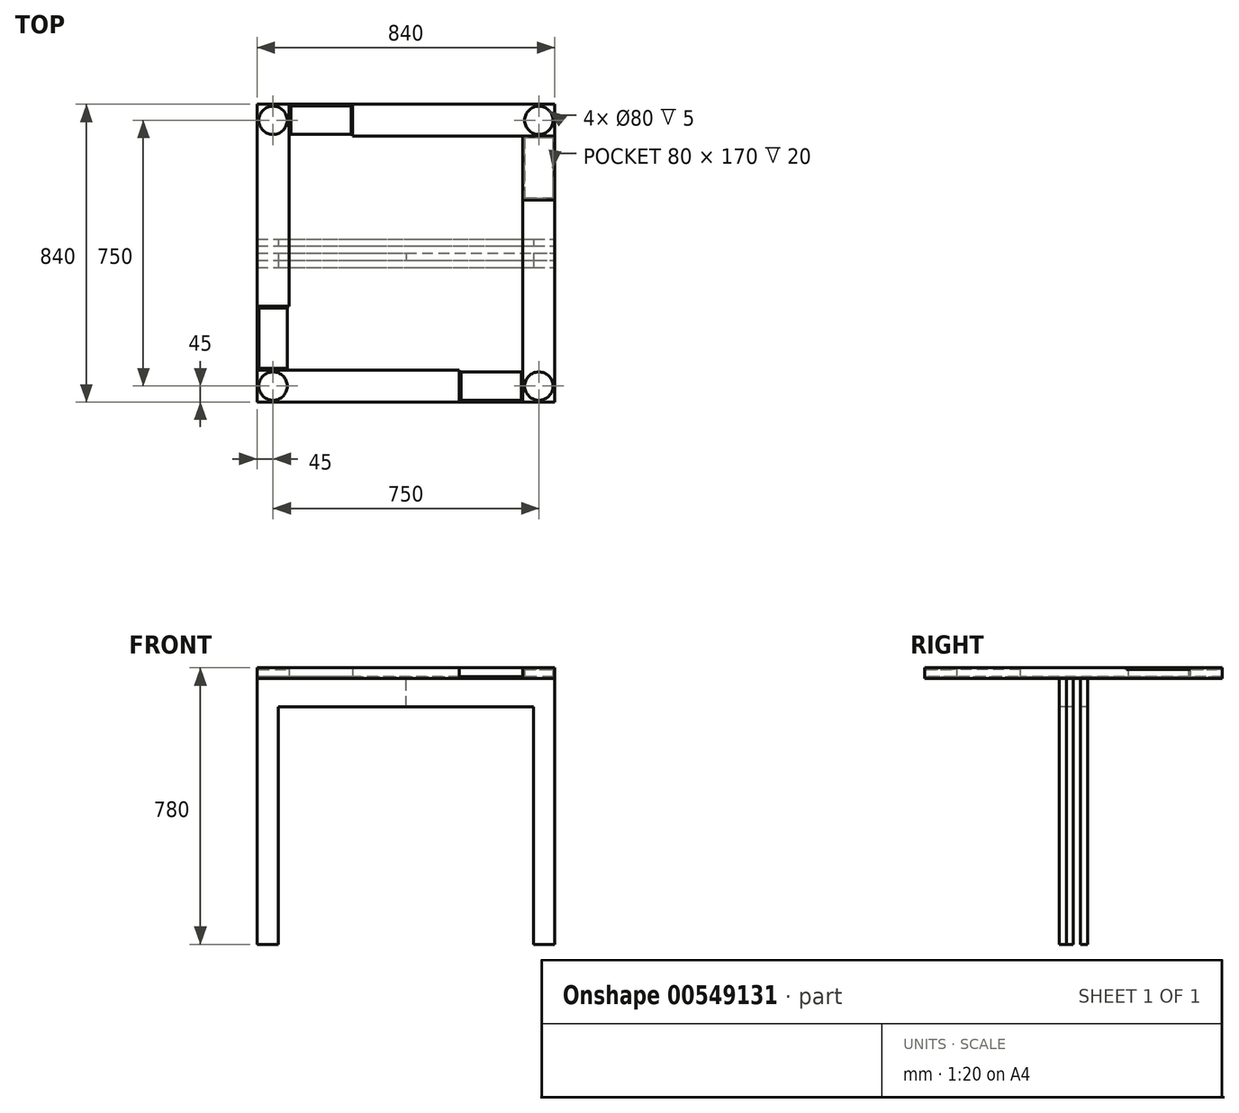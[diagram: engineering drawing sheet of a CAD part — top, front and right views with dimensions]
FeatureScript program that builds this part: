
annotation { "Feature Type Name" : "Feature", "Feature Type Description" : "" }
export const myFeature = defineFeature(function(context is Context, id is Id, definition is map)
    precondition{}
    {
        {
            var Q0;
            Q0=qCreatedBy(makeId("Front.planeOp"),FACE);
            var sketch = newSketch(context, id + "F0", { "sketchPlane" : qUnion([Q0])});
            skLineSegment(sketch, "E0.bottom", {"start": v(420, -15) * mm, "end": v(-420, -15) * mm});
            skLineSegment(sketch, "E0.top", {"start": v(420, 15) * mm, "end": v(-420, 15) * mm});
            skLineSegment(sketch, "E0.left", {"start": v(420, -15) * mm, "end": v(420, 15) * mm});
            skLineSegment(sketch, "E0.right", {"start": v(-420, -15) * mm, "end": v(-420, 15) * mm});
            skPoint(sketch, "E0.middle", {"position": v(0, 0) * mm});
            skLineSegment(sketch, "E1.0", {"start": v(420, -10) * mm, "end": v(-420, -10) * mm});
            skSolve(sketch);
        }
        {
            var Q0;
            Q0=makeQuery(id+"F0.imprint","IMPRINT",FACE,{"disambiguationData":[TD([[makeQuery(id+"F0.imprint","IMPRINT",EDGE,{"derivedFrom":sQuery(id+"F0.wireOp",EDGE,"E0.bottom")}),-1.0]])]});
            extrude(context, id + "F1", {"entities" : qUnion([Q0]), "depth" : 420 * mm, "offsetDistance" : 25 * mm});
        }
        {
            var Q0;
            Q0=makeQuery(id+"F0.imprint","IMPRINT",FACE,{"disambiguationData":[TD([[makeQuery(id+"F0.imprint","IMPRINT",EDGE,{"derivedFrom":sQuery(id+"F0.wireOp",EDGE,"E0.bottom")}),-1.0]])]});
            extrude(context, id + "F2", {"entities" : qUnion([Q0]), "oppositeDirection" : true, "depth" : 420 * mm, "offsetDistance" : 25 * mm});
        }
        {
            var Q0;
            Q0=makeQuery(id+"F2.opExtrude","SWEPT_FACE",FACE,{"disambiguationData":[OSD([sQuery(id+"F0.wireOp",EDGE,"E0.bottom")])]});
            var sketch = newSketch(context, id + "F3", { "sketchPlane" : qUnion([Q0])});
            skLineSegment(sketch, "E2.bottom", {"start": v(330, -330) * mm, "end": v(-330, -330) * mm});
            skLineSegment(sketch, "E2.top", {"start": v(330, 330) * mm, "end": v(-330, 330) * mm});
            skLineSegment(sketch, "E2.left", {"start": v(330, -330) * mm, "end": v(330, 330) * mm});
            skLineSegment(sketch, "E2.right", {"start": v(-330, -330) * mm, "end": v(-330, 330) * mm});
            skPoint(sketch, "E2.middle", {"position": v(0, 0) * mm});
            skLineSegment(sketch, "E3.bottom", {"start": v(-150, -330) * mm, "end": v(-330, -330) * mm});
            skLineSegment(sketch, "E3.top", {"start": v(-150, -420) * mm, "end": v(-330, -420) * mm});
            skLineSegment(sketch, "E3.left", {"start": v(-150, -330) * mm, "end": v(-150, -420) * mm});
            skLineSegment(sketch, "E3.right", {"start": v(-330, -330) * mm, "end": v(-330, -420) * mm});
            skLineSegment(sketch, "E4.bottom", {"start": v(-330, 150) * mm, "end": v(-420, 150) * mm});
            skLineSegment(sketch, "E4.top", {"start": v(-330, 330) * mm, "end": v(-420, 330) * mm});
            skLineSegment(sketch, "E4.left", {"start": v(-330, 150) * mm, "end": v(-330, 330) * mm});
            skLineSegment(sketch, "E4.right", {"start": v(-420, 150) * mm, "end": v(-420, 330) * mm});
            skPoint(sketch, "E5.oppositeSnap0", {"position": v(420, -210) * mm});
            skLineSegment(sketch, "E5.bottom", {"start": v(330, -150) * mm, "end": v(420, -150) * mm});
            skLineSegment(sketch, "E5.top", {"start": v(330, -330) * mm, "end": v(420, -330) * mm});
            skLineSegment(sketch, "E5.left", {"start": v(330, -150) * mm, "end": v(330, -330) * mm});
            skLineSegment(sketch, "E5.right", {"start": v(420, -150) * mm, "end": v(420, -330) * mm});
            skLineSegment(sketch, "E6.bottom", {"start": v(-420, 420) * mm, "end": v(420, 420) * mm});
            skLineSegment(sketch, "E6.top", {"start": v(-420, -420) * mm, "end": v(420, -420) * mm});
            skLineSegment(sketch, "E6.left", {"start": v(-420, -420) * mm, "end": v(-420, 420) * mm});
            skLineSegment(sketch, "E6.right", {"start": v(420, -420) * mm, "end": v(420, 420) * mm});
            skLineSegment(sketch, "E7.bottom", {"start": v(330, 330) * mm, "end": v(150, 330) * mm});
            skLineSegment(sketch, "E7.top", {"start": v(330, 420) * mm, "end": v(150, 420) * mm});
            skLineSegment(sketch, "E7.left", {"start": v(330, 330) * mm, "end": v(330, 420) * mm});
            skLineSegment(sketch, "E7.right", {"start": v(150, 330) * mm, "end": v(150, 420) * mm});
            skLineSegment(sketch, "E8.0", {"start": v(325, 415) * mm, "end": v(155, 415) * mm});
            skLineSegment(sketch, "E8.1", {"start": v(325, 335) * mm, "end": v(325, 415) * mm});
            skLineSegment(sketch, "E8.2", {"start": v(325, 335) * mm, "end": v(155, 335) * mm});
            skLineSegment(sketch, "E8.3", {"start": v(155, 335) * mm, "end": v(155, 415) * mm});
            skLineSegment(sketch, "E9.0", {"start": v(-415, 155) * mm, "end": v(-415, 325) * mm});
            skLineSegment(sketch, "E9.1", {"start": v(-335, 155) * mm, "end": v(-415, 155) * mm});
            skLineSegment(sketch, "E9.2", {"start": v(-335, 155) * mm, "end": v(-335, 325) * mm});
            skLineSegment(sketch, "E9.3", {"start": v(-335, 325) * mm, "end": v(-415, 325) * mm});
            skLineSegment(sketch, "E10.0", {"start": v(-155, -415) * mm, "end": v(-325, -415) * mm});
            skLineSegment(sketch, "E10.1", {"start": v(-155, -335) * mm, "end": v(-155, -415) * mm});
            skLineSegment(sketch, "E10.2", {"start": v(-155, -335) * mm, "end": v(-325, -335) * mm});
            skLineSegment(sketch, "E10.3", {"start": v(-325, -335) * mm, "end": v(-325, -415) * mm});
            skLineSegment(sketch, "E11.0", {"start": v(335, -155) * mm, "end": v(415, -155) * mm});
            skLineSegment(sketch, "E11.1", {"start": v(335, -155) * mm, "end": v(335, -325) * mm});
            skLineSegment(sketch, "E11.2", {"start": v(335, -325) * mm, "end": v(415, -325) * mm});
            skLineSegment(sketch, "E11.3", {"start": v(415, -155) * mm, "end": v(415, -325) * mm});
            skCircle(sketch, "E12", {"center": v(-375, 375) * mm, "radius": 40 * mm});
            skPoint(sketch, "E12.centerSnap0", {"position": v(-375, 330) * mm});
            skCircle(sketch, "E13", {"center": v(375, 375) * mm, "radius": 40 * mm});
            skPoint(sketch, "E13.centerSnap0", {"position": v(330, 375) * mm});
            skPoint(sketch, "E14", {"position": v(375, -150) * mm});
            skCircle(sketch, "E15", {"center": v(375, -375) * mm, "radius": 40 * mm});
            skPoint(sketch, "E15.centerSnap0", {"position": v(-150, -375) * mm});
            skPoint(sketch, "E15.centerSnap1", {"position": v(375, -330) * mm});
            skCircle(sketch, "E16", {"center": v(-375, -375) * mm, "radius": 40 * mm});
            skPoint(sketch, "E16.centerSnap0", {"position": v(-375, 150) * mm});
            skPoint(sketch, "E16.centerSnap1", {"position": v(-330, -375) * mm});
            skSolve(sketch);
        }
        {
            var Q0;
            Q0=makeQuery(id+"F3.imprint","IMPRINT",FACE,{"disambiguationData":[TD([[makeQuery(id+"F3.imprint","IMPRINT",EDGE,{"derivedFrom":sQuery(id+"F3.wireOp",EDGE,"E2.bottom")}),1.0]])]});
            var Q1;
            {var subQ5=sQuery(id+"F3.wireOp",EDGE,"E3.right");Q1=makeQuery(id+"F3.imprint","IMPRINT",FACE,{"disambiguationData":[TD([[makeQuery(id+"F3.imprint","IMPRINT",EDGE,{"derivedFrom":subQ5}),-1.0]])]});}
            var Q2;
            {var subQ0=sQuery(id+"F3.wireOp",EDGE,"E5.bottom");Q2=makeQuery(id+"F3.imprint","IMPRINT",FACE,{"disambiguationData":[TD([[makeQuery(id+"F3.imprint","IMPRINT",EDGE,{"derivedFrom":subQ0}),1.0]])]});}
            var Q3;
            {var subQ1=sQuery(id+"F3.wireOp",EDGE,"E5.bottom");Q3=makeQuery(id+"F3.imprint","IMPRINT",FACE,{"disambiguationData":[TD([[makeQuery(id+"F3.imprint","IMPRINT",EDGE,{"derivedFrom":subQ1}),-1.0]])]});}
            var Q4;
            Q4=makeQuery(id+"F3.imprint","IMPRINT",FACE,{"disambiguationData":[TD([[makeQuery(id+"F3.imprint","IMPRINT",EDGE,{"derivedFrom":sQuery(id+"F3.wireOp",EDGE,"E3.bottom")}),1.0]])]});
            var Q5;
            Q5=makeQuery(id+"F3.imprint","IMPRINT",FACE,{"disambiguationData":[TD([[makeQuery(id+"F3.imprint","IMPRINT",EDGE,{"derivedFrom":sQuery(id+"F3.wireOp",EDGE,"E16")}),1.0]])]});
            var Q6;
            Q6=makeQuery(id+"F3.imprint","IMPRINT",FACE,{"disambiguationData":[TD([[makeQuery(id+"F3.imprint","IMPRINT",EDGE,{"derivedFrom":sQuery(id+"F3.wireOp",EDGE,"E15")}),1.0]])]});
            extrude(context, id + "F4", {"entities" : qUnion([Q0, Q1, Q2, Q3, Q4, Q5, Q6]), "operationType" : NewBodyOperationType.ADD, "oppositeDirection" : true, "depth" : 30 * mm, "offsetDistance" : 25 * mm});
        }
        {
            var Q0;
            {var subQ3=makeQuery(id+"F2.opExtrude","CAP_EDGE",EDGE,{"disambiguationData":[OSD([sQuery(id+"F0.wireOp",EDGE,"E0.bottom")])],"isStart":true});var subQ5=sQuery(id+"F3.wireOp",EDGE,"E6.left");var subQ7=makeQuery(id+"F3.imprint","INTERSECT",VERTEX,{"derivedFrom":[subQ3,subQ5]});Q0=makeQuery(id+"F3.imprint","IMPRINT",FACE,{"disambiguationData":[TD([[makeQuery(id+"F3.imprint","IMPRINT",EDGE,{"disambiguationData":[TD([[subQ7,-1.0]])],"derivedFrom":subQ5}),-1.0]])]});}
            var Q1;
            {var subQ6=sQuery(id+"F3.wireOp",EDGE,"E2.top");Q1=makeQuery(id+"F3.imprint","IMPRINT",FACE,{"disambiguationData":[TD([[makeQuery(id+"F3.imprint","IMPRINT",EDGE,{"derivedFrom":subQ6}),-1.0]])]});}
            var Q2;
            {var subQ5=sQuery(id+"F3.wireOp",EDGE,"E7.left");Q2=makeQuery(id+"F3.imprint","IMPRINT",FACE,{"disambiguationData":[TD([[makeQuery(id+"F3.imprint","IMPRINT",EDGE,{"derivedFrom":subQ5}),-1.0]])]});}
            var Q3;
            Q3=makeQuery(id+"F3.imprint","IMPRINT",FACE,{"disambiguationData":[TD([[makeQuery(id+"F3.imprint","IMPRINT",EDGE,{"derivedFrom":sQuery(id+"F3.wireOp",EDGE,"E12")}),1.0]])]});
            var Q4;
            Q4=makeQuery(id+"F3.imprint","IMPRINT",FACE,{"disambiguationData":[TD([[makeQuery(id+"F3.imprint","IMPRINT",EDGE,{"derivedFrom":sQuery(id+"F3.wireOp",EDGE,"E13")}),1.0]])]});
            var Q5;
            {var subQ0=sQuery(id+"F3.wireOp",EDGE,"E4.left");Q5=makeQuery(id+"F3.imprint","IMPRINT",FACE,{"disambiguationData":[TD([[makeQuery(id+"F3.imprint","IMPRINT",EDGE,{"derivedFrom":subQ0}),1.0]])]});}
            var Q6;
            Q6=makeQuery(id+"F3.imprint","IMPRINT",FACE,{"disambiguationData":[TD([[makeQuery(id+"F3.imprint","IMPRINT",EDGE,{"derivedFrom":sQuery(id+"F3.wireOp",EDGE,"E7.bottom")}),-1.0]])]});
            var Q7;
            {var subQ0=sQuery(id+"F3.wireOp",EDGE,"kfzZb0uT-yHJu-uCjX-pyc7-7eUP6x9U4umR.bottom");var subQ1=sQuery(id+"F3.wireOp",EDGE,"E2.top");var subQ2=sQuery(id+"F3.wireOp",EDGE,"E5.left");var subQ3=sQuery(id+"F3.wireOp",EDGE,"E2.left");var subQ4=sQuery(id+"F3.wireOp",EDGE,"E4.left");var subQ5=sQuery(id+"F3.wireOp",EDGE,"E2.right");Q7=makeQuery(id+"F4.boolean.opBoolean","COPY",FACE,{"disambiguationData":[TD([makeQuery(id+"F4.opExtrude","SWEPT_FACE",FACE,{"disambiguationData":[OSD([subQ1,subQ0])]})])],"derivedFrom":makeQuery(id+"F4.opExtrude","CAP_FACE",FACE,{"disambiguationData":[OSD([sQuery(id+"F3.wireOp",EDGE,"E2.bottom"),subQ1,subQ3,subQ5,sQuery(id+"F3.wireOp",EDGE,"E3.bottom"),subQ0,subQ4,subQ2])],"isStart":false})});}
            extrude(context, id + "F5", {"entities" : qUnion([Q0, Q1, Q2, Q3, Q4, Q5, Q6]), "operationType" : NewBodyOperationType.ADD, "oppositeDirection" : true, "depth" : 30 * mm, "endBoundEntityFace" : qUnion([Q7]), "offsetDistance" : 25 * mm});
        }
        {
            var Q0;
            {var subQ1=sQuery(id+"F3.wireOp",EDGE,"E4.bottom");Q0=makeQuery(id+"F3.imprint","IMPRINT",FACE,{"disambiguationData":[TD([[makeQuery(id+"F3.imprint","IMPRINT",EDGE,{"derivedFrom":subQ1}),-1.0]])]});}
            var Q1;
            Q1=makeQuery(id+"F3.imprint","IMPRINT",FACE,{"disambiguationData":[TD([[makeQuery(id+"F3.imprint","IMPRINT",EDGE,{"derivedFrom":sQuery(id+"F3.wireOp",EDGE,"E9.0")}),-1.0]])]});
            var Q2;
            Q2=makeQuery(id+"F3.imprint","IMPRINT",FACE,{"disambiguationData":[TD([[makeQuery(id+"F3.imprint","IMPRINT",EDGE,{"derivedFrom":sQuery(id+"F3.wireOp",EDGE,"E8.0")}),1.0]])]});
            var Q3;
            Q3=makeQuery(id+"F3.imprint","IMPRINT",FACE,{"disambiguationData":[TD([[makeQuery(id+"F3.imprint","IMPRINT",EDGE,{"derivedFrom":sQuery(id+"F3.wireOp",EDGE,"E7.bottom")}),-1.0]])]});
            var Q4;
            {var subQ1=sQuery(id+"F3.wireOp",EDGE,"E5.bottom");Q4=makeQuery(id+"F3.imprint","IMPRINT",FACE,{"disambiguationData":[TD([[makeQuery(id+"F3.imprint","IMPRINT",EDGE,{"derivedFrom":subQ1}),-1.0]])]});}
            var Q5;
            Q5=makeQuery(id+"F3.imprint","IMPRINT",FACE,{"disambiguationData":[TD([[makeQuery(id+"F3.imprint","IMPRINT",EDGE,{"derivedFrom":sQuery(id+"F3.wireOp",EDGE,"E11.0")}),-1.0]])]});
            var Q6;
            Q6=makeQuery(id+"F3.imprint","IMPRINT",FACE,{"disambiguationData":[TD([[makeQuery(id+"F3.imprint","IMPRINT",EDGE,{"derivedFrom":sQuery(id+"F3.wireOp",EDGE,"E3.bottom")}),1.0]])]});
            var Q7;
            Q7=makeQuery(id+"F3.imprint","IMPRINT",FACE,{"disambiguationData":[TD([[makeQuery(id+"F3.imprint","IMPRINT",EDGE,{"derivedFrom":sQuery(id+"F3.wireOp",EDGE,"E10.0")}),-1.0]])]});
            var Q8;
            Q8=makeQuery(id+"F3.imprint","IMPRINT",FACE,{"disambiguationData":[TD([[makeQuery(id+"F3.imprint","IMPRINT",EDGE,{"derivedFrom":sQuery(id+"F3.wireOp",EDGE,"E12")}),1.0]])]});
            var Q9;
            Q9=makeQuery(id+"F3.imprint","IMPRINT",FACE,{"disambiguationData":[TD([[makeQuery(id+"F3.imprint","IMPRINT",EDGE,{"derivedFrom":sQuery(id+"F3.wireOp",EDGE,"E16")}),1.0]])]});
            var Q10;
            Q10=makeQuery(id+"F3.imprint","IMPRINT",FACE,{"disambiguationData":[TD([[makeQuery(id+"F3.imprint","IMPRINT",EDGE,{"derivedFrom":sQuery(id+"F3.wireOp",EDGE,"E15")}),1.0]])]});
            var Q11;
            Q11=makeQuery(id+"F3.imprint","IMPRINT",FACE,{"disambiguationData":[TD([[makeQuery(id+"F3.imprint","IMPRINT",EDGE,{"derivedFrom":sQuery(id+"F3.wireOp",EDGE,"E13")}),1.0]])]});
            var Q12;
            {var subQ0=sQuery(id+"F3.wireOp",EDGE,"E4.left");Q12=makeQuery(id+"F3.imprint","IMPRINT",FACE,{"disambiguationData":[TD([[makeQuery(id+"F3.imprint","IMPRINT",EDGE,{"derivedFrom":subQ0}),1.0]])]});}
            extrude(context, id + "F6", {"entities" : qUnion([Q0, Q1, Q2, Q3, Q4, Q5, Q6, Q7, Q8, Q9, Q10, Q11, Q12]), "oppositeDirection" : true, "depth" : 5 * mm, "offsetDistance" : 25 * mm});
        }
        {
            var Q0;
            Q0=makeQuery(id+"F6.opExtrude","SWEPT_BODY",BODY,{"disambiguationData":[OSD([sQuery(id+"F3.wireOp",EDGE,"E3.bottom"),sQuery(id+"F3.wireOp",EDGE,"E3.left"),sQuery(id+"F3.wireOp",EDGE,"E3.right"),sQuery(id+"F3.wireOp",EDGE,"E6.top")])]});
            var Q1;
            Q1=makeQuery(id+"F6.opExtrude","SWEPT_BODY",BODY,{"disambiguationData":[OSD([sQuery(id+"F3.wireOp",EDGE,"E4.bottom"),sQuery(id+"F3.wireOp",EDGE,"E4.top"),sQuery(id+"F3.wireOp",EDGE,"E4.left"),sQuery(id+"F3.wireOp",EDGE,"E6.left")])]});
            var Q2;
            Q2=makeQuery(id+"F6.opExtrude","SWEPT_BODY",BODY,{"disambiguationData":[OSD([sQuery(id+"F3.wireOp",EDGE,"E5.bottom"),sQuery(id+"F3.wireOp",EDGE,"E5.top"),sQuery(id+"F3.wireOp",EDGE,"E5.left"),sQuery(id+"F3.wireOp",EDGE,"E6.right")])]});
            var Q3;
            Q3=makeQuery(id+"F6.opExtrude","SWEPT_BODY",BODY,{"disambiguationData":[OSD([sQuery(id+"F3.wireOp",EDGE,"E7.bottom"),sQuery(id+"F3.wireOp",EDGE,"E7.top"),sQuery(id+"F3.wireOp",EDGE,"E7.left"),sQuery(id+"F3.wireOp",EDGE,"E7.right")])]});
            var Q4;
            Q4=makeQuery(id+"F6.opExtrude","SWEPT_BODY",BODY,{"disambiguationData":[OSD([sQuery(id+"F3.wireOp",EDGE,"E16")])]});
            var Q5;
            Q5=makeQuery(id+"F6.opExtrude","SWEPT_BODY",BODY,{"disambiguationData":[OSD([sQuery(id+"F3.wireOp",EDGE,"E12")])]});
            var Q6;
            Q6=makeQuery(id+"F6.opExtrude","SWEPT_BODY",BODY,{"disambiguationData":[OSD([sQuery(id+"F3.wireOp",EDGE,"E13")])]});
            var Q7;
            Q7=makeQuery(id+"F6.opExtrude","SWEPT_BODY",BODY,{"disambiguationData":[OSD([sQuery(id+"F3.wireOp",EDGE,"E15")])]});
            transform(context, id + "F7", {"entities" : qUnion([Q0, Q1, Q2, Q3, Q4, Q5, Q6, Q7]), "transformType" : TransformType.TRANSLATION_3D, "dx" : 0 * mm, "dy" : 0 * mm, "dz" : 25 * mm, "makeCopy" : false});
        }
        {
            var Q0;
            Q0=makeQuery(id+"F6.opExtrude","SWEPT_BODY",BODY,{"disambiguationData":[OSD([sQuery(id+"F3.wireOp",EDGE,"E3.bottom"),sQuery(id+"F3.wireOp",EDGE,"E3.left"),sQuery(id+"F3.wireOp",EDGE,"E3.right"),sQuery(id+"F3.wireOp",EDGE,"E6.top")])]});
            var Q1;
            Q1=makeQuery(id+"F6.opExtrude","SWEPT_BODY",BODY,{"disambiguationData":[OSD([sQuery(id+"F3.wireOp",EDGE,"E5.bottom"),sQuery(id+"F3.wireOp",EDGE,"E5.top"),sQuery(id+"F3.wireOp",EDGE,"E5.left"),sQuery(id+"F3.wireOp",EDGE,"E6.right")])]});
            var Q2;
            Q2=makeQuery(id+"F6.opExtrude","SWEPT_BODY",BODY,{"disambiguationData":[OSD([sQuery(id+"F3.wireOp",EDGE,"E7.bottom"),sQuery(id+"F3.wireOp",EDGE,"E7.top"),sQuery(id+"F3.wireOp",EDGE,"E7.left"),sQuery(id+"F3.wireOp",EDGE,"E7.right")])]});
            var Q3;
            Q3=makeQuery(id+"F6.opExtrude","SWEPT_BODY",BODY,{"disambiguationData":[OSD([sQuery(id+"F3.wireOp",EDGE,"E4.bottom"),sQuery(id+"F3.wireOp",EDGE,"E4.top"),sQuery(id+"F3.wireOp",EDGE,"E4.left"),sQuery(id+"F3.wireOp",EDGE,"E6.left")])]});
            var Q4;
            Q4=makeQuery(id+"F2.opExtrude","SWEPT_BODY",BODY,{"disambiguationData":[OSD([sQuery(id+"F0.wireOp",EDGE,"E0.bottom"),sQuery(id+"F0.wireOp",EDGE,"E0.left"),sQuery(id+"F0.wireOp",EDGE,"E0.right"),sQuery(id+"F0.wireOp",EDGE,"E1.0")])]});
            var Q5;
            Q5=makeQuery(id+"F1.opExtrude","SWEPT_BODY",BODY,{"disambiguationData":[OSD([sQuery(id+"F0.wireOp",EDGE,"E0.bottom"),sQuery(id+"F0.wireOp",EDGE,"E0.left"),sQuery(id+"F0.wireOp",EDGE,"E0.right"),sQuery(id+"F0.wireOp",EDGE,"E1.0")])]});
            booleanBodies(context, id + "F8", {"operationType" : BooleanOperationType.SUBTRACTION, "tools" : qUnion([Q0, Q1, Q2, Q3]), "targets" : qUnion([Q4, Q5]), "keepTools" : true});
        }
        {
            var Q0;
            Q0=makeQuery(id+"F6.opExtrude","SWEPT_BODY",BODY,{"disambiguationData":[OSD([sQuery(id+"F3.wireOp",EDGE,"E15")])]});
            var Q1;
            Q1=makeQuery(id+"F6.opExtrude","SWEPT_BODY",BODY,{"disambiguationData":[OSD([sQuery(id+"F3.wireOp",EDGE,"E16")])]});
            var Q2;
            Q2=makeQuery(id+"F6.opExtrude","SWEPT_BODY",BODY,{"disambiguationData":[OSD([sQuery(id+"F3.wireOp",EDGE,"E12")])]});
            var Q3;
            Q3=makeQuery(id+"F6.opExtrude","SWEPT_BODY",BODY,{"disambiguationData":[OSD([sQuery(id+"F3.wireOp",EDGE,"E13")])]});
            var Q4;
            Q4=makeQuery(id+"F2.opExtrude","SWEPT_BODY",BODY,{"disambiguationData":[OSD([sQuery(id+"F0.wireOp",EDGE,"E0.bottom"),sQuery(id+"F0.wireOp",EDGE,"E0.left"),sQuery(id+"F0.wireOp",EDGE,"E0.right"),sQuery(id+"F0.wireOp",EDGE,"E1.0")])]});
            var Q5;
            Q5=makeQuery(id+"F1.opExtrude","SWEPT_BODY",BODY,{"disambiguationData":[OSD([sQuery(id+"F0.wireOp",EDGE,"E0.bottom"),sQuery(id+"F0.wireOp",EDGE,"E0.left"),sQuery(id+"F0.wireOp",EDGE,"E0.right"),sQuery(id+"F0.wireOp",EDGE,"E1.0")])]});
            booleanBodies(context, id + "F9", {"operationType" : BooleanOperationType.SUBTRACTION, "tools" : qUnion([Q0, Q1, Q2, Q3]), "targets" : qUnion([Q4, Q5])});
        }
        {
            var Q0;
            Q0=makeQuery(id+"F2.opExtrude","SWEPT_FACE",FACE,{"disambiguationData":[OSD([sQuery(id+"F0.wireOp",EDGE,"E0.bottom")])]});
            var sketch = newSketch(context, id + "F10", { "sketchPlane" : qUnion([Q0])});
            skPoint(sketch, "E17.oppositeSnap0", {"position": v(0, 0) * mm});
            skLineSegment(sketch, "E17.bottom", {"start": v(-420, 0) * mm, "end": v(0, 0) * mm});
            skLineSegment(sketch, "E17.top", {"start": v(-420, 20) * mm, "end": v(0, 20) * mm});
            skLineSegment(sketch, "E17.left", {"start": v(-420, 0) * mm, "end": v(-420, 20) * mm});
            skLineSegment(sketch, "E17.right", {"start": v(0, 0) * mm, "end": v(0, 20) * mm});
            skLineSegment(sketch, "E18.bottom", {"start": v(0, 20) * mm, "end": v(420, 20) * mm});
            skLineSegment(sketch, "E18.top", {"start": v(0, 0) * mm, "end": v(420, 0) * mm});
            skLineSegment(sketch, "E18.left", {"start": v(0, 20) * mm, "end": v(0, 0) * mm});
            skLineSegment(sketch, "E18.right", {"start": v(420, 20) * mm, "end": v(420, 0) * mm});
            skLineSegment(sketch, "E19.top", {"start": v(-420, -20) * mm, "end": v(0, -20) * mm});
            skLineSegment(sketch, "E19.left", {"start": v(-420, 0) * mm, "end": v(-420, -20) * mm});
            skLineSegment(sketch, "E19.right", {"start": v(0, 0) * mm, "end": v(0, -20) * mm});
            skLineSegment(sketch, "E20.bottom", {"start": v(0, -20) * mm, "end": v(420, -20) * mm});
            skLineSegment(sketch, "E20.left", {"start": v(0, -20) * mm, "end": v(0, 0) * mm});
            skLineSegment(sketch, "E20.right", {"start": v(420, -20) * mm, "end": v(420, 0) * mm});
            skLineSegment(sketch, "E21.bottom", {"start": v(-420, -20) * mm, "end": v(420, -20) * mm});
            skLineSegment(sketch, "E21.top", {"start": v(-420, -40) * mm, "end": v(420, -40) * mm});
            skLineSegment(sketch, "E21.left", {"start": v(-420, -20) * mm, "end": v(-420, -40) * mm});
            skLineSegment(sketch, "E21.right", {"start": v(420, -20) * mm, "end": v(420, -40) * mm});
            skLineSegment(sketch, "E22.bottom", {"start": v(-420, 20) * mm, "end": v(420, 20) * mm});
            skLineSegment(sketch, "E22.top", {"start": v(-420, 40) * mm, "end": v(420, 40) * mm});
            skLineSegment(sketch, "E22.left", {"start": v(-420, 20) * mm, "end": v(-420, 40) * mm});
            skLineSegment(sketch, "E22.right", {"start": v(420, 20) * mm, "end": v(420, 40) * mm});
            skSolve(sketch);
        }
        {
            var Q0;
            Q0=makeQuery(id+"F10.imprint","IMPRINT",FACE,{"disambiguationData":[TD([[makeQuery(id+"F10.imprint","IMPRINT",EDGE,{"derivedFrom":sQuery(id+"F10.wireOp",EDGE,"E22.top")}),-1.0]])]});
            var Q1;
            Q1=makeQuery(id+"F10.imprint","IMPRINT",FACE,{"disambiguationData":[TD([[makeQuery(id+"F10.imprint","IMPRINT",EDGE,{"derivedFrom":sQuery(id+"F10.wireOp",EDGE,"E21.top")}),1.0]])]});
            extrude(context, id + "F11", {"entities" : qUnion([Q0, Q1]), "depth" : 750 * mm, "offsetDistance" : 25 * mm});
        }
        {
            var Q0;
            {var subQ0=sQuery(id+"F10.wireOp",EDGE,"E17.left");Q0=makeQuery(id+"F10.imprint","IMPRINT",FACE,{"disambiguationData":[TD([[makeQuery(id+"F10.imprint","IMPRINT",EDGE,{"derivedFrom":subQ0}),-1.0]])]});}
            var Q1;
            Q1=makeQuery(id+"F10.imprint","IMPRINT",FACE,{"disambiguationData":[TD([[makeQuery(id+"F10.imprint","IMPRINT",EDGE,{"derivedFrom":sQuery(id+"F10.wireOp",EDGE,"E18.top")}),1.0]])]});
            var Q2;
            {var subQ0=sQuery(id+"F10.wireOp",EDGE,"E22.bottom");var subQ1=sQuery(id+"F10.wireOp",EDGE,"E22.right");var subQ2=sQuery(id+"F10.wireOp",EDGE,"E22.top");Q2=makeQuery(id+"F15.boolean.opBoolean","SPLIT",FACE,{"disambiguationData":[TD([makeQuery(id+"F11.opExtrude","SWEPT_FACE",FACE,{"disambiguationData":[OSD([subQ1])]})])],"derivedFrom":makeQuery(id+"F11.opExtrude","CAP_FACE",FACE,{"disambiguationData":[OSD([subQ0,subQ2,sQuery(id+"F10.wireOp",EDGE,"E22.left"),subQ1])],"isStart":false})});}
            extrude(context, id + "F12", {"entities" : qUnion([Q0, Q1]), "endBound" : BoundingType.UP_TO_SURFACE, "depth" : 25 * mm, "endBoundEntityFace" : qUnion([Q2]), "offsetDistance" : 25 * mm});
        }
        {
            var Q0;
            {var subQ0=sQuery(id+"F10.wireOp",EDGE,"E18.left");Q0=makeQuery(id+"F10.imprint","IMPRINT",FACE,{"disambiguationData":[TD([[makeQuery(id+"F10.imprint","IMPRINT",EDGE,{"derivedFrom":subQ0}),1.0]])]});}
            var Q1;
            Q1=makeQuery(id+"F10.imprint","IMPRINT",FACE,{"disambiguationData":[TD([[makeQuery(id+"F10.imprint","IMPRINT",EDGE,{"derivedFrom":sQuery(id+"F10.wireOp",EDGE,"E17.bottom")}),1.0]])]});
            var Q2;
            {var subQ0=sQuery(id+"F10.wireOp",EDGE,"E21.bottom");var subQ1=sQuery(id+"F10.wireOp",EDGE,"E21.right");var subQ2=sQuery(id+"F10.wireOp",EDGE,"E21.top");Q2=makeQuery(id+"F15.boolean.opBoolean","SPLIT",FACE,{"disambiguationData":[TD([makeQuery(id+"F11.opExtrude","SWEPT_FACE",FACE,{"disambiguationData":[OSD([subQ1])]})])],"derivedFrom":makeQuery(id+"F11.opExtrude","CAP_FACE",FACE,{"disambiguationData":[OSD([subQ0,subQ2,sQuery(id+"F10.wireOp",EDGE,"E21.left"),subQ1])],"isStart":false})});}
            extrude(context, id + "F13", {"entities" : qUnion([Q0, Q1]), "endBound" : BoundingType.UP_TO_SURFACE, "depth" : 25 * mm, "endBoundEntityFace" : qUnion([Q2]), "offsetDistance" : 25 * mm});
        }
        {
            var Q0;
            Q0=makeQuery(id+"F11.opExtrude","SWEPT_FACE",FACE,{"disambiguationData":[OSD([sQuery(id+"F10.wireOp",EDGE,"E22.top")])]});
            var sketch = newSketch(context, id + "F14", { "sketchPlane" : qUnion([Q0])});
            skLineSegment(sketch, "E23.bottom", {"start": v(-360, -765) * mm, "end": v(360, -765) * mm});
            skLineSegment(sketch, "E23.top", {"start": v(-360, -95) * mm, "end": v(360, -95) * mm});
            skLineSegment(sketch, "E23.left", {"start": v(-360, -765) * mm, "end": v(-360, -95) * mm});
            skLineSegment(sketch, "E23.right", {"start": v(360, -765) * mm, "end": v(360, -95) * mm});
            skPoint(sketch, "E24", {"position": v(0, -765) * mm});
            skSolve(sketch);
        }
        {
            var Q0;
            Q0=makeQuery(id+"F14.imprint","IMPRINT",FACE,{"disambiguationData":[TD([[makeQuery(id+"F14.imprint","IMPRINT",EDGE,{"derivedFrom":sQuery(id+"F14.wireOp",EDGE,"E23.bottom")}),1.0]])]});
            extrude(context, id + "F15", {"entities" : qUnion([Q0]), "operationType" : NewBodyOperationType.REMOVE, "oppositeDirection" : true, "depth" : 201 * mm, "offsetDistance" : 25 * mm});
        }
    });
